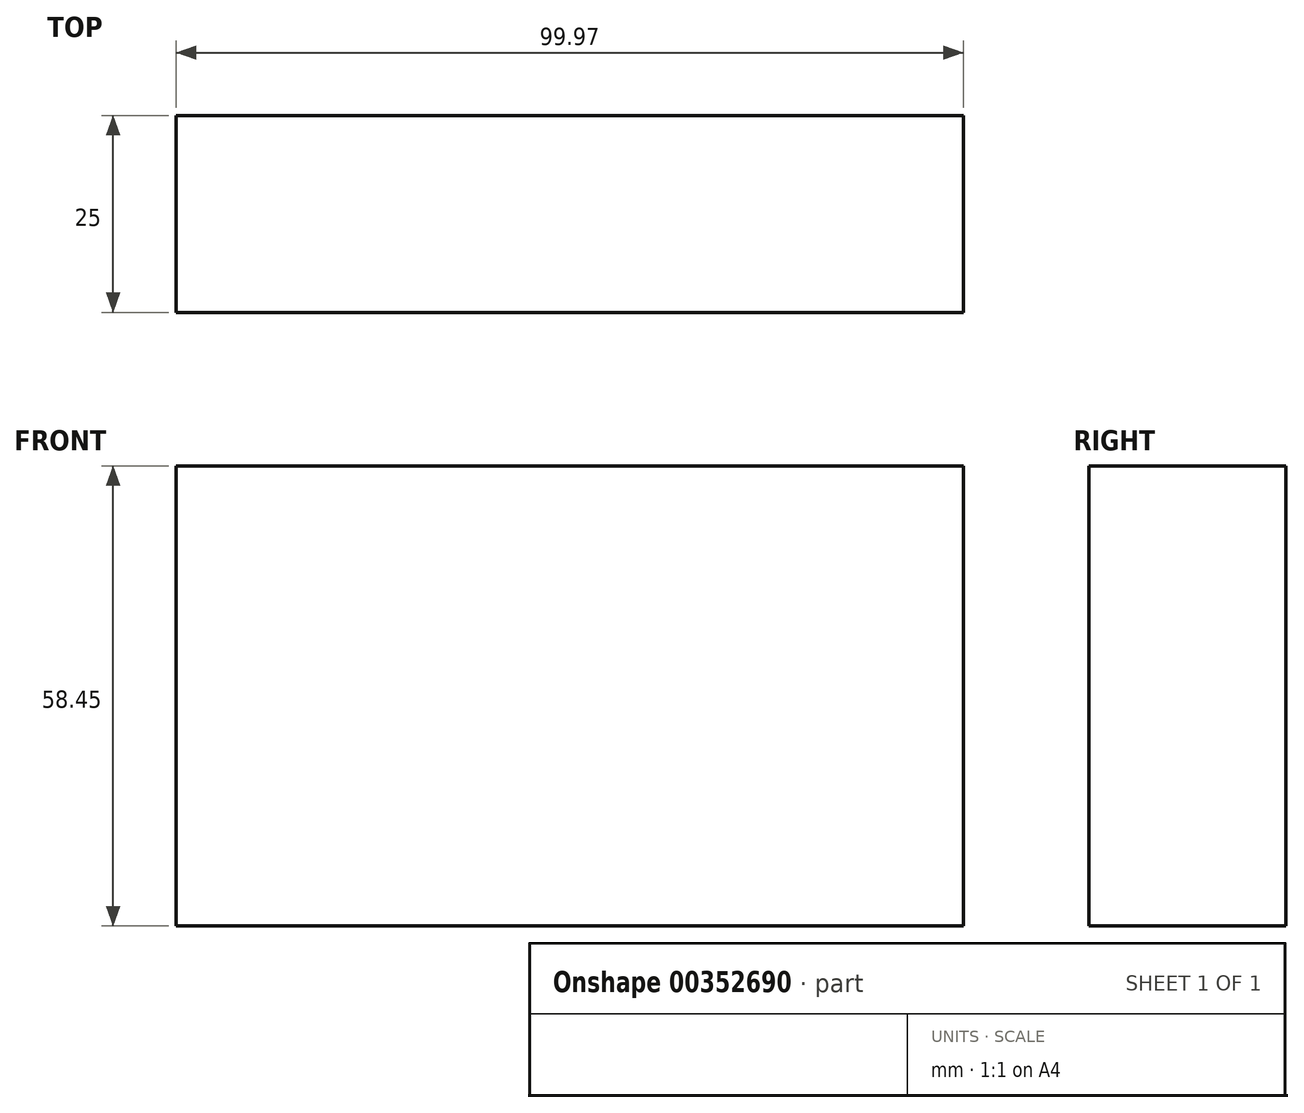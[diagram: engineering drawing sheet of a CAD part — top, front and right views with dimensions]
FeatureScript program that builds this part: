
annotation { "Feature Type Name" : "Feature", "Feature Type Description" : "" }
export const myFeature = defineFeature(function(context is Context, id is Id, definition is map)
    precondition{}
    {
        {
            var Q0;
            Q0=qCreatedBy(makeId("Front.planeOp"),FACE);
            var sketch = newSketch(context, id + "F0", { "sketchPlane" : qUnion([Q0])});
            skLineSegment(sketch, "E0.bottom", {"start": v(-103.05, 16.99) * mm, "end": v(-3.08, 16.99) * mm});
            skLineSegment(sketch, "E0.top", {"start": v(-103.05, -41.46) * mm, "end": v(-3.08, -41.46) * mm});
            skLineSegment(sketch, "E0.left", {"start": v(-103.05, 16.99) * mm, "end": v(-103.05, -41.46) * mm});
            skLineSegment(sketch, "E0.right", {"start": v(-3.08, 16.99) * mm, "end": v(-3.08, -41.46) * mm});
            skSolve(sketch);
        }
        {
            var Q0;
            Q0=makeQuery(id+"F0.imprint","IMPRINT",FACE,{"disambiguationData":[TD([[makeQuery(id+"F0.imprint","IMPRINT",EDGE,{"derivedFrom":sQuery(id+"F0.wireOp",EDGE,"E0.bottom")}),-1.0]])]});
            extrude(context, id + "F1", {"entities" : qUnion([Q0]), "depth" : 25 * mm});
        }
    });
